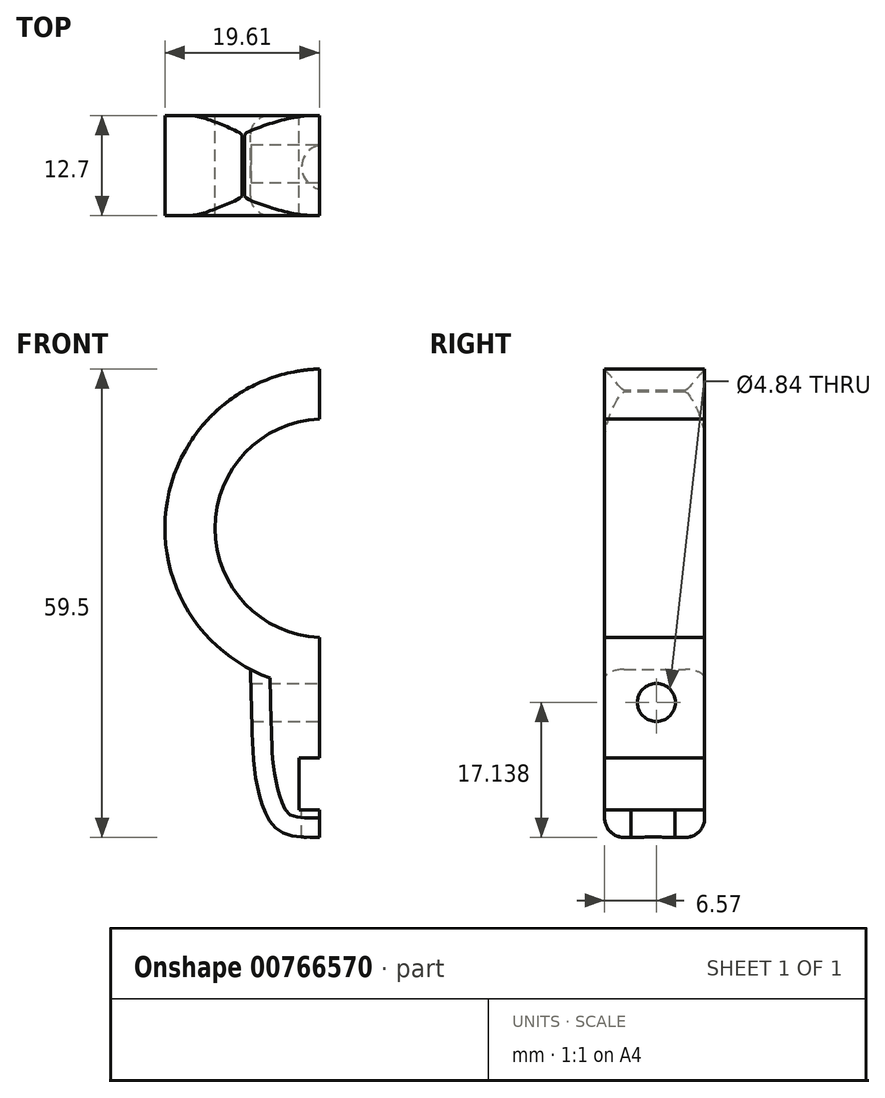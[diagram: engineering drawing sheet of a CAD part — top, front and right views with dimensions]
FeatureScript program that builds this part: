
annotation { "Feature Type Name" : "Feature", "Feature Type Description" : "" }
export const myFeature = defineFeature(function(context is Context, id is Id, definition is map)
    precondition{}
    {
        {
            var Q0;
            Q0=qCreatedBy(makeId("Front.planeOp"),FACE);
            var sketch = newSketch(context, id + "F0", { "sketchPlane" : qUnion([Q0])});
            skCircle(sketch, "E0", {"center": v(0, 0) * mm, "radius": 13.9 * mm});
            skCircle(sketch, "E1.0", {"center": v(0, 0) * mm, "radius": 20.24 * mm});
            skFitSpline(sketch, "E2", {"points": [v(-10.48, 17.32) * mm, v(-6.62, 22.45) * mm, v(-5.79, 30.49) * mm, v(0, 31.88) * mm, v(5.12, 30.56) * mm, v(6.08, 23.46) * mm, v(9.7, 17.76) * mm], "startDerivative": vector(26.15, 14.41) * mm, "endDerivative": vector(40.23, -23.63) * mm});
            skFitSpline(sketch, "E3", {"points": [v(-9.4, -17.93) * mm, v(-8.61, -32.2) * mm, v(-6.2, -38.09) * mm, v(0, -39.27) * mm, v(6.65, -38) * mm, v(9.7, -28.64) * mm, v(9.7, -17.76) * mm], "startDerivative": vector(4.47, -161.39) * mm, "endDerivative": vector(-1.33, 64.22) * mm});
            skLineSegment(sketch, "E4.bottom", {"start": v(-3.24, -35.81) * mm, "end": v(3.24, -35.81) * mm});
            skLineSegment(sketch, "E4.top", {"start": v(-3.24, -29.16) * mm, "end": v(3.24, -29.16) * mm});
            skLineSegment(sketch, "E4.left", {"start": v(-3.24, -35.81) * mm, "end": v(-3.24, -29.16) * mm});
            skLineSegment(sketch, "E4.right", {"start": v(3.24, -35.81) * mm, "end": v(3.24, -29.16) * mm});
            skSolve(sketch);
        }
        {
            var Q0;
            Q0=makeQuery(id+"F0.imprint","IMPRINT",FACE,{"disambiguationData":[TD([[makeQuery(id+"F0.imprint","IMPRINT",EDGE,{"derivedFrom":sQuery(id+"F0.wireOp",EDGE,"E0")}),-1.0]])]});
            var Q1;
            {var subQ0=sQuery(id+"F0.wireOp",EDGE,"E3");Q1=makeQuery(id+"F0.imprint","IMPRINT",FACE,{"disambiguationData":[TD([[makeQuery(id+"F0.imprint","IMPRINT",EDGE,{"derivedFrom":subQ0}),1.0]])]});}
            var Q2;
            {var subQ0=sQuery(id+"F0.wireOp",EDGE,"E2");var subQ1=sQuery(id+"F0.wireOp",EDGE,"E1.0");var subQ2=makeQuery(id+"F0.imprint","INTERSECT",VERTEX,{"disambiguationData":[OD(1.0)],"derivedFrom":[subQ1,subQ0]});Q2=makeQuery(id+"F0.imprint","IMPRINT",FACE,{"disambiguationData":[TD([[makeQuery(id+"F0.imprint","IMPRINT",EDGE,{"disambiguationData":[TD([[subQ2,-1.0]])],"derivedFrom":subQ1}),-1.0]])]});}
            extrude(context, id + "F1", {"entities" : qUnion([Q0, Q1, Q2]), "depth" : 12.7 * mm, "offsetDistance" : 25.4 * mm});
        }
        {
            var Q0;
            Q0=qCreatedBy(makeId("Right.planeOp"),FACE);
            var sketch = newSketch(context, id + "F2", { "sketchPlane" : qUnion([Q0])});
            skCircle(sketch, "E5", {"center": v(-6.29, 25.64) * mm, "radius": 1.9 * mm});
            skCircle(sketch, "E6", {"center": v(-6.13, -22.13) * mm, "radius": 2.42 * mm});
            skSolve(sketch);
        }
        {
            var Q0;
            Q0 = qSketchRegion(id + "F2", true);
            extrude(context, id + "F3", {"entities" : qUnion([Q0]), "operationType" : NewBodyOperationType.REMOVE, "endBound" : BoundingType.SYMMETRIC, "oppositeDirection" : true, "depth" : 25.4 * mm, "offsetDistance" : 25.4 * mm});
        }
        {
            var Q0;
            Q0=qCreatedBy(makeId("Top.planeOp"),FACE);
            cPlane(context, id + "F4", {"entities" : qUnion([Q0]), "cplaneType" : CPlaneType.OFFSET, "offset" : 30.84 * mm, "oppositeDirection" : true, "width" : 152.4 * mm, "height" : 152.4 * mm});
        }
        {
            var Q0;
            Q0=qCreatedBy(id+"F4.planeOp",FACE);
            var sketch = newSketch(context, id + "F5", { "sketchPlane" : qUnion([Q0])});
            skCircle(sketch, "E7", {"center": v(0, -6.56) * mm, "radius": 2.87 * mm});
            skSolve(sketch);
        }
        {
            var Q0;
            Q0=makeQuery(id+"F5.imprint","IMPRINT",FACE,{"disambiguationData":[TD([[makeQuery(id+"F5.imprint","IMPRINT",EDGE,{"derivedFrom":sQuery(id+"F5.wireOp",EDGE,"E7")}),1.0]])]});
            extrude(context, id + "F6", {"entities" : qUnion([Q0]), "operationType" : NewBodyOperationType.REMOVE, "oppositeDirection" : true, "depth" : 25.4 * mm, "offsetDistance" : 25.4 * mm});
        }
        {
            var Q0;
            Q0=qCreatedBy(makeId("Front.planeOp"),FACE);
            var sketch = newSketch(context, id + "F7", { "sketchPlane" : qUnion([Q0])});
            skLineSegment(sketch, "E8.bottom", {"start": v(-0.64, 36.94) * mm, "end": v(30.33, 36.94) * mm});
            skLineSegment(sketch, "E8.top", {"start": v(-0.64, -46.33) * mm, "end": v(30.33, -46.33) * mm});
            skLineSegment(sketch, "E8.left", {"start": v(-0.64, 36.94) * mm, "end": v(-0.64, -46.33) * mm});
            skLineSegment(sketch, "E8.right", {"start": v(30.33, 36.94) * mm, "end": v(30.33, -46.33) * mm});
            skSolve(sketch);
        }
        {
            var Q0;
            Q0=makeQuery(id+"F7.imprint","IMPRINT",FACE,{"disambiguationData":[TD([[makeQuery(id+"F7.imprint","IMPRINT",EDGE,{"derivedFrom":sQuery(id+"F7.wireOp",EDGE,"E8.bottom")}),-1.0]])]});
            extrude(context, id + "F8", {"entities" : qUnion([Q0]), "operationType" : NewBodyOperationType.REMOVE, "depth" : 25.4 * mm, "offsetDistance" : 25.4 * mm});
        }
        {
            var Q0;
            Q0=makeQuery(id+"F1.opExtrude","CAP_EDGE",EDGE,{"disambiguationData":[OSD([sQuery(id+"F0.wireOp",EDGE,"E2")])],"isStart":false});
            var Q1;
            {var subQ0=sQuery(id+"F0.wireOp",EDGE,"E1.0");Q1=makeQuery(id+"F1.opExtrude","CAP_EDGE",EDGE,{"disambiguationData":[OSD([subQ0]),TDD([makeQuery(id+"F0.imprint","IMPRINT",EDGE,{"disambiguationData":[TD([[makeQuery(id+"F0.imprint","INTERSECT",VERTEX,{"disambiguationData":[OD(0.0)],"derivedFrom":[subQ0,sQuery(id+"F0.wireOp",EDGE,"E2")]}),-1.0]])],"derivedFrom":subQ0})])],"isStart":false});}
            var Q2;
            Q2=makeQuery(id+"F1.opExtrude","CAP_EDGE",EDGE,{"disambiguationData":[OSD([sQuery(id+"F0.wireOp",EDGE,"E3")])],"isStart":false});
            var Q3;
            Q3=makeQuery(id+"F1.opExtrude","CAP_EDGE",EDGE,{"disambiguationData":[OSD([sQuery(id+"F0.wireOp",EDGE,"E2")])],"isStart":true});
            var Q4;
            {var subQ0=sQuery(id+"F0.wireOp",EDGE,"E1.0");Q4=makeQuery(id+"F1.opExtrude","CAP_EDGE",EDGE,{"disambiguationData":[OSD([subQ0]),TDD([makeQuery(id+"F0.imprint","IMPRINT",EDGE,{"disambiguationData":[TD([[makeQuery(id+"F0.imprint","INTERSECT",VERTEX,{"disambiguationData":[OD(0.0)],"derivedFrom":[subQ0,sQuery(id+"F0.wireOp",EDGE,"E2")]}),-1.0]])],"derivedFrom":subQ0})])],"isStart":true});}
            var Q5;
            Q5=makeQuery(id+"F1.opExtrude","CAP_EDGE",EDGE,{"disambiguationData":[OSD([sQuery(id+"F0.wireOp",EDGE,"E3")])],"isStart":true});
            fillet(context, id + "F9", {"entities" : qUnion([Q0, Q1, Q2, Q3, Q4, Q5]), "radius" : 2.45 * mm, "tangentPropagation" : true, "allowEdgeOverflow" : false});
        }
    });
